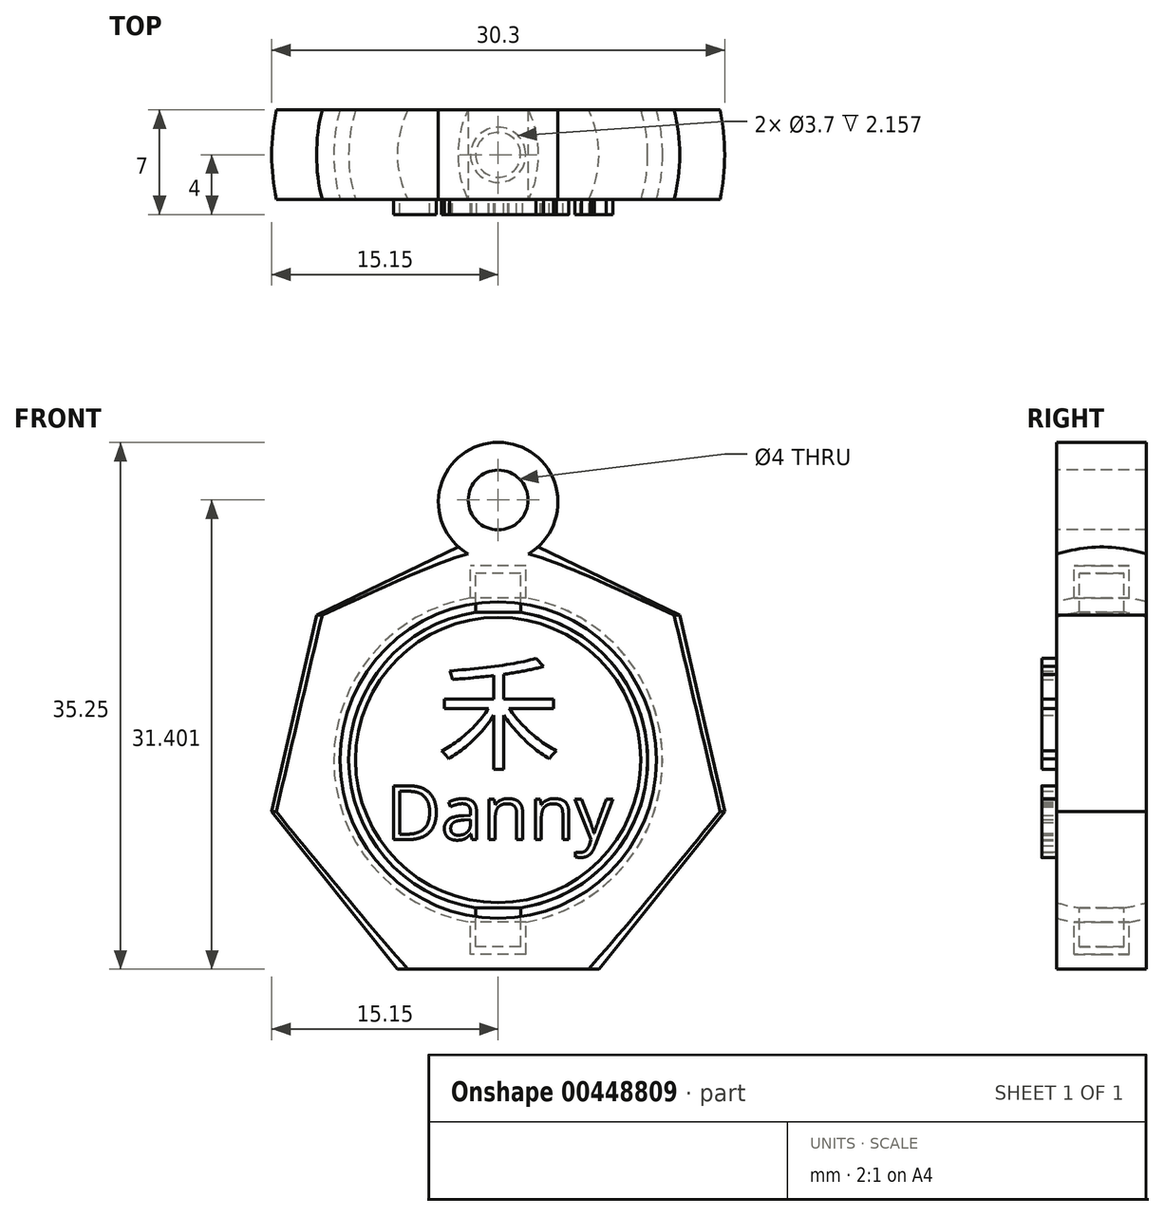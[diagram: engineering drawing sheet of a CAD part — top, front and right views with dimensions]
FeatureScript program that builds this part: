
annotation { "Feature Type Name" : "Feature", "Feature Type Description" : "" }
export const myFeature = defineFeature(function(context is Context, id is Id, definition is map)
    precondition{}
    {
        {
            var Q0;
            Q0=qCreatedBy(makeId("Front.planeOp"),FACE);
            var sketch = newSketch(context, id + "F0", { "sketchPlane" : qUnion([Q0])});
            skLineSegment(sketch, "E0.bottom", {"start": v(1.85, -13) * mm, "end": v(-1.85, -13) * mm});
            skLineSegment(sketch, "E0.top", {"start": v(1.85, 13) * mm, "end": v(-1.85, 13) * mm});
            skLineSegment(sketch, "E0.left", {"start": v(1.85, -13) * mm, "end": v(1.85, 13) * mm});
            skLineSegment(sketch, "E0.right", {"start": v(-1.85, -13) * mm, "end": v(-1.85, 13) * mm});
            skPoint(sketch, "E0.middle", {"position": v(0, 0) * mm});
            skLineSegment(sketch, "E1.bottom", {"start": v(1.5, -12.5) * mm, "end": v(-1.5, -12.5) * mm});
            skLineSegment(sketch, "E1.top", {"start": v(1.5, 12.5) * mm, "end": v(-1.5, 12.5) * mm});
            skLineSegment(sketch, "E1.left", {"start": v(1.5, -12.5) * mm, "end": v(1.5, 12.5) * mm});
            skLineSegment(sketch, "E1.right", {"start": v(-1.5, -12.5) * mm, "end": v(-1.5, 12.5) * mm});
            skCircle(sketch, "E2", {"center": v(0, 0) * mm, "radius": 10 * mm});
            skCircle(sketch, "E3", {"center": v(0, 0) * mm, "radius": 11 * mm});
            skCircle(sketch, "E4.cCircle", {"center": v(0, 0) * mm, "radius": 14 * mm, "construction": true});
            skLineSegment(sketch, "E4.0", {"start": v(15.15, -3.46) * mm, "end": v(6.74, -14) * mm});
            skLineSegment(sketch, "E4.1", {"start": v(6.74, -14) * mm, "end": v(-6.74, -14) * mm});
            skLineSegment(sketch, "E4.2", {"start": v(-6.74, -14) * mm, "end": v(-15.15, -3.46) * mm});
            skLineSegment(sketch, "E4.3", {"start": v(-15.15, -3.46) * mm, "end": v(-12.15, 9.69) * mm});
            skLineSegment(sketch, "E4.4", {"start": v(-12.15, 9.69) * mm, "end": v(0, 15.54) * mm});
            skLineSegment(sketch, "E4.5", {"start": v(0, 15.54) * mm, "end": v(12.15, 9.69) * mm});
            skLineSegment(sketch, "E4.6", {"start": v(12.15, 9.69) * mm, "end": v(15.15, -3.46) * mm});
            skPoint(sketch, "E4.0.midPoint", {"position": v(10.95, -8.73) * mm});
            skSolve(sketch);
        }
        {
            var Q0;
            Q0=qCreatedBy(makeId("Front.planeOp"),FACE);
            var sketch = newSketch(context, id + "F1", { "sketchPlane" : qUnion([Q0])});
            skLineSegment(sketch, "E5.0", {"start": v(-6.74, -14) * mm, "end": v(-15.15, -3.46) * mm});
            skLineSegment(sketch, "E5.1", {"start": v(12.15, 9.69) * mm, "end": v(15.15, -3.46) * mm});
            skLineSegment(sketch, "E5.2", {"start": v(-15.15, -3.46) * mm, "end": v(-12.15, 9.69) * mm});
            skLineSegment(sketch, "E5.3", {"start": v(-12.15, 9.69) * mm, "end": v(0, 15.54) * mm});
            skLineSegment(sketch, "E5.4", {"start": v(1.85, -13) * mm, "end": v(-1.85, -13) * mm});
            skLineSegment(sketch, "E5.5", {"start": v(1.85, 13) * mm, "end": v(-1.85, 13) * mm});
            skLineSegment(sketch, "E5.6", {"start": v(1.85, -13) * mm, "end": v(1.85, -10.84) * mm});
            skLineSegment(sketch, "E5.7", {"start": v(-1.85, -13) * mm, "end": v(-1.85, -10.84) * mm});
            skLineSegment(sketch, "E5.8", {"start": v(1.5, -12.5) * mm, "end": v(-1.5, -12.5) * mm});
            skLineSegment(sketch, "E5.9", {"start": v(1.5, 12.5) * mm, "end": v(-1.5, 12.5) * mm});
            skLineSegment(sketch, "E5.10", {"start": v(1.5, -12.5) * mm, "end": v(1.5, -9.89) * mm});
            skLineSegment(sketch, "E5.11", {"start": v(-1.5, -12.5) * mm, "end": v(-1.5, -9.89) * mm});
            skArc(sketch, "E5.12", {"start": v(-1.5, 9.89) * mm, "mid": v(-10, 0) * mm, "end": v(-1.5, -9.89) * mm});
            skArc(sketch, "E5.13", {"start": v(-1.85, 10.84) * mm, "mid": v(-11, 0) * mm, "end": v(-1.85, -10.84) * mm});
            skLineSegment(sketch, "E5.15", {"start": v(15.15, -3.46) * mm, "end": v(6.74, -14) * mm});
            skLineSegment(sketch, "E5.16", {"start": v(6.74, -14) * mm, "end": v(-6.74, -14) * mm});
            skLineSegment(sketch, "E5.17", {"start": v(0, 15.54) * mm, "end": v(12.15, 9.69) * mm});
            skLineSegment(sketch, "E6.trimOffspring", {"start": v(-1.5, 9.89) * mm, "end": v(-1.5, 12.5) * mm});
            skLineSegment(sketch, "E7.trimOffspring", {"start": v(-1.85, 10.84) * mm, "end": v(-1.85, 13) * mm});
            skLineSegment(sketch, "E8.trimOffspring", {"start": v(1.5, 9.89) * mm, "end": v(1.5, 12.5) * mm});
            skLineSegment(sketch, "E9.trimOffspring", {"start": v(1.85, 10.84) * mm, "end": v(1.85, 13) * mm});
            skArc(sketch, "E10.trimOffspring", {"start": v(1.5, -9.89) * mm, "mid": v(10, 0) * mm, "end": v(1.5, 9.89) * mm});
            skArc(sketch, "E11.trimOffspring", {"start": v(1.85, -10.84) * mm, "mid": v(11, 0) * mm, "end": v(1.85, 10.84) * mm});
            skSolve(sketch);
        }
        {
            var Q0;
            Q0=qCreatedBy(makeId("Front.planeOp"),FACE);
            var sketch = newSketch(context, id + "F2", { "sketchPlane" : qUnion([Q0])});
            skLineSegment(sketch, "E12.0", {"start": v(-6.74, -14) * mm, "end": v(-15.15, -3.46) * mm});
            skLineSegment(sketch, "E12.1", {"start": v(12.15, 9.69) * mm, "end": v(15.15, -3.46) * mm});
            skLineSegment(sketch, "E12.2", {"start": v(-15.15, -3.46) * mm, "end": v(-12.15, 9.69) * mm});
            skLineSegment(sketch, "E12.3", {"start": v(-12.15, 9.69) * mm, "end": v(0, 15.54) * mm});
            skLineSegment(sketch, "E12.4", {"start": v(1.85, -13) * mm, "end": v(-1.85, -13) * mm});
            skLineSegment(sketch, "E12.5", {"start": v(1.85, 13) * mm, "end": v(-1.85, 13) * mm});
            skLineSegment(sketch, "E12.6", {"start": v(1.85, -13) * mm, "end": v(1.85, -10.84) * mm});
            skLineSegment(sketch, "E12.7", {"start": v(-1.85, -13) * mm, "end": v(-1.85, -10.84) * mm});
            skLineSegment(sketch, "E12.8", {"start": v(1.5, -12.5) * mm, "end": v(-1.5, -12.5) * mm});
            skLineSegment(sketch, "E12.9", {"start": v(1.5, 12.5) * mm, "end": v(-1.5, 12.5) * mm});
            skLineSegment(sketch, "E12.10", {"start": v(1.5, -12.5) * mm, "end": v(1.5, -9.89) * mm});
            skLineSegment(sketch, "E12.11", {"start": v(-1.5, -12.5) * mm, "end": v(-1.5, -9.89) * mm});
            skArc(sketch, "E12.12", {"start": v(-1.5, 9.89) * mm, "mid": v(-10, 0) * mm, "end": v(-1.5, -9.89) * mm});
            skArc(sketch, "E12.13", {"start": v(-1.85, 10.84) * mm, "mid": v(-11, 0) * mm, "end": v(-1.85, -10.84) * mm});
            skLineSegment(sketch, "E12.14", {"start": v(15.15, -3.46) * mm, "end": v(6.74, -14) * mm});
            skLineSegment(sketch, "E12.15", {"start": v(6.74, -14) * mm, "end": v(-6.74, -14) * mm});
            skLineSegment(sketch, "E12.16", {"start": v(0, 15.54) * mm, "end": v(12.15, 9.69) * mm});
            skLineSegment(sketch, "E12.17", {"start": v(-1.5, 9.89) * mm, "end": v(-1.5, 12.5) * mm});
            skLineSegment(sketch, "E12.18", {"start": v(-1.85, 10.84) * mm, "end": v(-1.85, 13) * mm});
            skLineSegment(sketch, "E12.19", {"start": v(1.5, 9.89) * mm, "end": v(1.5, 12.5) * mm});
            skLineSegment(sketch, "E12.20", {"start": v(1.85, 10.84) * mm, "end": v(1.85, 13) * mm});
            skArc(sketch, "E12.21", {"start": v(1.5, -9.89) * mm, "mid": v(10, 0) * mm, "end": v(1.5, 9.89) * mm});
            skArc(sketch, "E12.22", {"start": v(1.85, -10.84) * mm, "mid": v(11, 0) * mm, "end": v(1.85, 10.84) * mm});
            skLineSegment(sketch, "E13", {"start": v(0, 15.54) * mm, "end": v(0, -14) * mm});
            skSolve(sketch);
        }
        {
            var Q0;
            Q0=qCreatedBy(makeId("Front.planeOp"),FACE);
            var sketch = newSketch(context, id + "F3", { "sketchPlane" : qUnion([Q0])});
            skLineSegment(sketch, "E14.1", {"start": v(12.15, 9.69) * mm, "end": v(15.15, -3.46) * mm});
            skLineSegment(sketch, "E14.4", {"start": v(1.85, -13) * mm, "end": v(0, -13) * mm});
            skLineSegment(sketch, "E14.5", {"start": v(1.85, 13) * mm, "end": v(0, 13) * mm});
            skLineSegment(sketch, "E14.6", {"start": v(1.85, -13) * mm, "end": v(1.85, -10.84) * mm});
            skLineSegment(sketch, "E14.8", {"start": v(1.5, -12.5) * mm, "end": v(0, -12.5) * mm});
            skLineSegment(sketch, "E14.9", {"start": v(1.5, 12.5) * mm, "end": v(0, 12.5) * mm});
            skLineSegment(sketch, "E14.10", {"start": v(1.5, -12.5) * mm, "end": v(1.5, -9.89) * mm});
            skLineSegment(sketch, "E14.14", {"start": v(15.15, -3.46) * mm, "end": v(6.74, -14) * mm});
            skLineSegment(sketch, "E14.15", {"start": v(6.74, -14) * mm, "end": v(0, -14) * mm});
            skLineSegment(sketch, "E14.16", {"start": v(0, 15.54) * mm, "end": v(12.15, 9.69) * mm});
            skLineSegment(sketch, "E14.19", {"start": v(1.5, 9.89) * mm, "end": v(1.5, 12.5) * mm});
            skLineSegment(sketch, "E14.20", {"start": v(1.85, 10.84) * mm, "end": v(1.85, 13) * mm});
            skArc(sketch, "E14.21", {"start": v(1.5, -9.89) * mm, "mid": v(10, 0) * mm, "end": v(1.5, 9.89) * mm});
            skArc(sketch, "E14.22", {"start": v(1.85, -10.84) * mm, "mid": v(11, 0) * mm, "end": v(1.85, 10.84) * mm});
            skLineSegment(sketch, "E14.23", {"start": v(0, 15.54) * mm, "end": v(0, 13) * mm});
            skPoint(sketch, "E14.3.end.orphan", {"position": v(0, 15.54) * mm});
            skPoint(sketch, "E14.3.start.orphan", {"position": v(-12.15, 9.69) * mm});
            skPoint(sketch, "E14.17.end.orphan", {"position": v(-1.5, 12.5) * mm});
            skPoint(sketch, "E14.17.start.orphan", {"position": v(-1.5, 9.89) * mm});
            skPoint(sketch, "E14.18.end.orphan", {"position": v(-1.85, 13) * mm});
            skPoint(sketch, "E14.18.start.orphan", {"position": v(-1.85, 10.84) * mm});
            skPoint(sketch, "E14.13.end.orphan", {"position": v(-1.85, -10.84) * mm});
            skPoint(sketch, "E14.13.start.orphan", {"position": v(-1.85, 10.84) * mm});
            skPoint(sketch, "E14.12.end.orphan", {"position": v(-1.5, -9.89) * mm});
            skPoint(sketch, "E14.12.start.orphan", {"position": v(-1.5, 9.89) * mm});
            skPoint(sketch, "E14.2.end.orphan", {"position": v(-12.15, 9.69) * mm});
            skPoint(sketch, "E14.2.start.orphan", {"position": v(-15.15, -3.46) * mm});
            skLineSegment(sketch, "E15.trimOffspring", {"start": v(0, 12.5) * mm, "end": v(0, -12.5) * mm});
            skPoint(sketch, "E14.0.end.orphan", {"position": v(-15.15, -3.46) * mm});
            skPoint(sketch, "E14.0.start.orphan", {"position": v(-6.74, -14) * mm});
            skPoint(sketch, "E14.11.end.orphan", {"position": v(-1.5, -9.89) * mm});
            skPoint(sketch, "E14.11.start.orphan", {"position": v(-1.5, -12.5) * mm});
            skPoint(sketch, "E14.7.end.orphan", {"position": v(-1.85, -10.84) * mm});
            skPoint(sketch, "E14.7.start.orphan", {"position": v(-1.85, -13) * mm});
            skLineSegment(sketch, "E16.trimOffspring", {"start": v(0, -13) * mm, "end": v(0, -14) * mm});
            skSolve(sketch);
        }
        {
            var Q0;
            Q0=qSketchRegion(id+"F3",true);
            var Q1;
            Q1=sQuery(id+"F3.wireOp",EDGE,"E15.trimOffspring");
            revolve(context, id + "F4", {"entities" : qUnion([Q0]), "axis" : qUnion([Q1]), "revolveType" : RevolveType.FULL});
        }
        {
            var Q0;
            Q0=qCreatedBy(makeId("Right.planeOp"),FACE);
            var sketch = newSketch(context, id + "F5", { "sketchPlane" : qUnion([Q0])});
            skLineSegment(sketch, "E17.bottom", {"start": v(3, 20.08) * mm, "end": v(25.6, 20.08) * mm});
            skLineSegment(sketch, "E17.top", {"start": v(3, -19.17) * mm, "end": v(25.6, -19.17) * mm});
            skLineSegment(sketch, "E17.left", {"start": v(3, 20.08) * mm, "end": v(3, -19.17) * mm});
            skLineSegment(sketch, "E17.right", {"start": v(25.6, 20.08) * mm, "end": v(25.6, -19.17) * mm});
            skLineSegment(sketch, "E18.MirrorCS", {"start": v(-3, 20.08) * mm, "end": v(-25.6, 20.08) * mm});
            skLineSegment(sketch, "E19.MirrorCS", {"start": v(-3, -19.17) * mm, "end": v(-25.6, -19.17) * mm});
            skLineSegment(sketch, "E20.MirrorCS", {"start": v(-3, 20.08) * mm, "end": v(-3, -19.17) * mm});
            skLineSegment(sketch, "E21.MirrorCS", {"start": v(-25.6, 20.08) * mm, "end": v(-25.6, -19.17) * mm});
            skSolve(sketch);
        }
        {
            var Q0;
            Q0=qSketchRegion(id+"F5",true);
            extrude(context, id + "F6", {"entities" : qUnion([Q0]), "operationType" : NewBodyOperationType.REMOVE, "endBound" : BoundingType.SYMMETRIC, "oppositeDirection" : true, "depth" : 60 * mm});
        }
        {
            var Q0;
            Q0=qCreatedBy(makeId("Front.planeOp"),FACE);
            var sketch = newSketch(context, id + "F7", { "sketchPlane" : qUnion([Q0])});
            skText(sketch, "E22", { "text": "禾", "fontName": "NotoSansCJKjp-Regular.otf"});
            const initialGuessF7  = {"E22": [-0.00412, 0, 1, 0, 0.006]};
            skSetInitialGuess(sketch, initialGuessF7);
            skSolve(sketch);
        }
        {
            var Q0;
            Q0=qSketchRegion(id+"F7",true);
            extrude(context, id + "F8", {"entities" : qUnion([Q0]), "operationType" : NewBodyOperationType.ADD, "depth" : 4 * mm});
        }
        {
            var Q0;
            Q0=qCreatedBy(makeId("Front.planeOp"),FACE);
            var sketch = newSketch(context, id + "F9", { "sketchPlane" : qUnion([Q0])});
            skText(sketch, "E23", { "text": "Danny", "fontName": "OpenSans-Regular.ttf"});
            const initialGuessF9  = {"E23": [-0.0075, -0.00532, 1, 0, 0.00362]};
            skSetInitialGuess(sketch, initialGuessF9);
            skSolve(sketch);
        }
        {
            var Q0;
            Q0=qSketchRegion(id+"F9",true);
            extrude(context, id + "F10", {"entities" : qUnion([Q0]), "operationType" : NewBodyOperationType.ADD, "depth" : 4 * mm});
        }
        {
            var Q0;
            Q0=qCreatedBy(makeId("Front.planeOp"),FACE);
            var sketch = newSketch(context, id + "F11", { "sketchPlane" : qUnion([Q0])});
            skCircle(sketch, "E24", {"center": v(0, 17.25) * mm, "radius": 4 * mm});
            skSolve(sketch);
        }
        {
            var Q0;
            Q0=qSketchRegion(id+"F11",true);
            extrude(context, id + "F12", {"entities" : qUnion([Q0]), "operationType" : NewBodyOperationType.ADD, "endBound" : BoundingType.SYMMETRIC, "depth" : 6 * mm});
        }
        {
            var Q0;
            Q0=qCreatedBy(makeId("Front.planeOp"),FACE);
            var sketch = newSketch(context, id + "F13", { "sketchPlane" : qUnion([Q0])});
            skCircle(sketch, "E25", {"center": v(0, 17.4) * mm, "radius": 2 * mm});
            skSolve(sketch);
        }
        {
            var Q0;
            Q0=qSketchRegion(id+"F13",true);
            extrude(context, id + "F14", {"entities" : qUnion([Q0]), "operationType" : NewBodyOperationType.REMOVE, "endBound" : BoundingType.SYMMETRIC, "oppositeDirection" : true, "depth" : 25 * mm});
        }
    });
